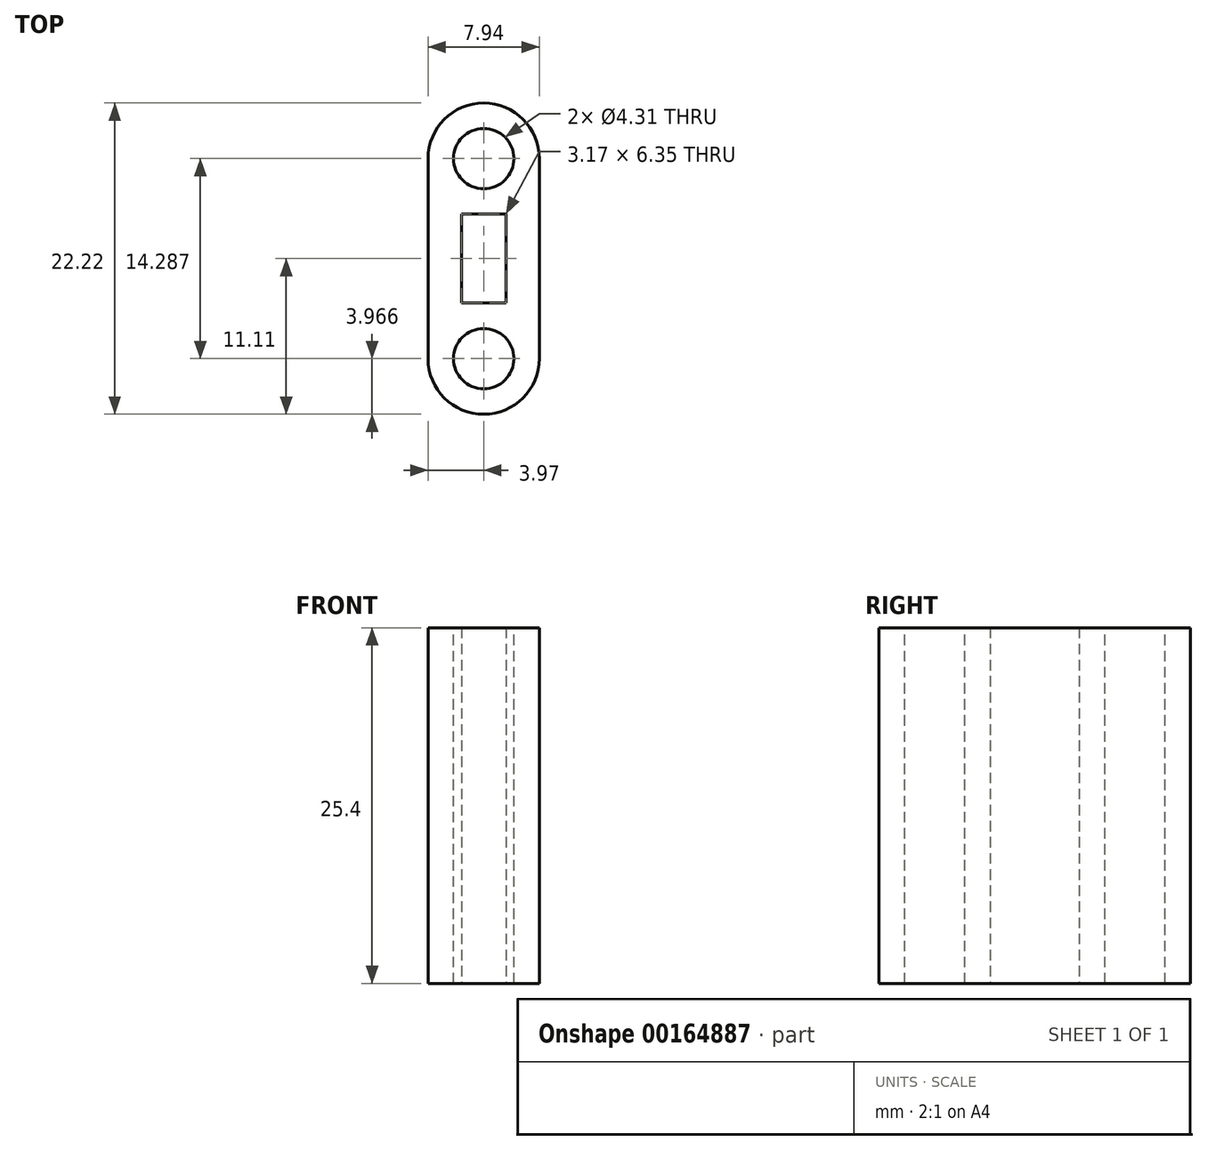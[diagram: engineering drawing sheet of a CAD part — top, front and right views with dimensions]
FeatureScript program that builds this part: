
annotation { "Feature Type Name" : "Feature", "Feature Type Description" : "" }
export const myFeature = defineFeature(function(context is Context, id is Id, definition is map)
    precondition{}
    {
        {
            var Q0;
            Q0=qCreatedBy(makeId("Top.planeOp"),FACE);
            var sketch = newSketch(context, id + "F0", { "sketchPlane" : qUnion([Q0])});
            skLineSegment(sketch, "E0.bottom", {"start": v(3.97, 11.11) * mm, "end": v(-3.97, 11.11) * mm});
            skLineSegment(sketch, "E0.top", {"start": v(3.97, -11.11) * mm, "end": v(-3.97, -11.11) * mm});
            skLineSegment(sketch, "E0.left", {"start": v(3.97, 11.11) * mm, "end": v(3.97, -11.11) * mm});
            skLineSegment(sketch, "E0.right", {"start": v(-3.97, 11.11) * mm, "end": v(-3.97, -11.11) * mm});
            skPoint(sketch, "E0.middle", {"position": v(0, 0) * mm});
            skLineSegment(sketch, "E1.bottom", {"start": v(1.59, 3.18) * mm, "end": v(-1.59, 3.18) * mm});
            skLineSegment(sketch, "E1.top", {"start": v(1.59, -3.18) * mm, "end": v(-1.59, -3.18) * mm});
            skLineSegment(sketch, "E1.left", {"start": v(1.59, 3.18) * mm, "end": v(1.59, -3.18) * mm});
            skLineSegment(sketch, "E1.right", {"start": v(-1.59, 3.18) * mm, "end": v(-1.59, -3.18) * mm});
            skSolve(sketch);
        }
        {
            var Q0;
            Q0 = qSketchRegion(id + "F0", true);
            extrude(context, id + "F1", {"entities" : qUnion([Q0]), "depth" : 25.4 * mm});
        }
        {
            var Q0;
            Q0=makeQuery(id+"F1.opExtrude","CAP_FACE",FACE,{"disambiguationData":[OSD([sQuery(id+"F0.wireOp",EDGE,"E0.bottom"),sQuery(id+"F0.wireOp",EDGE,"E0.top"),sQuery(id+"F0.wireOp",EDGE,"E0.left"),sQuery(id+"F0.wireOp",EDGE,"E0.right"),sQuery(id+"F0.wireOp",EDGE,"E1.bottom"),sQuery(id+"F0.wireOp",EDGE,"E1.top"),sQuery(id+"F0.wireOp",EDGE,"E1.left"),sQuery(id+"F0.wireOp",EDGE,"E1.right")])],"isStart":false});
            var sketch = newSketch(context, id + "F2", { "sketchPlane" : qUnion([Q0])});
            skLineSegment(sketch, "E2.bottom", {"start": v(0, 11.11) * mm, "end": v(3.97, 11.11) * mm, "construction": true});
            skLineSegment(sketch, "E2.top", {"start": v(0, 7.14) * mm, "end": v(3.97, 7.14) * mm, "construction": true});
            skLineSegment(sketch, "E2.left", {"start": v(0, 11.11) * mm, "end": v(0, 7.14) * mm, "construction": true});
            skLineSegment(sketch, "E2.right", {"start": v(3.97, 11.11) * mm, "end": v(3.97, 7.14) * mm, "construction": true});
            skLineSegment(sketch, "E3.bottom", {"start": v(0, -11.11) * mm, "end": v(3.97, -11.11) * mm, "construction": true});
            skLineSegment(sketch, "E3.top", {"start": v(0, -7.14) * mm, "end": v(3.97, -7.14) * mm, "construction": true});
            skLineSegment(sketch, "E3.left", {"start": v(0, -11.11) * mm, "end": v(0, -7.14) * mm, "construction": true});
            skLineSegment(sketch, "E3.right", {"start": v(3.97, -11.11) * mm, "end": v(3.97, -7.14) * mm, "construction": true});
            skCircle(sketch, "E4", {"center": v(0, 7.14) * mm, "radius": 2.15 * mm});
            skCircle(sketch, "E5", {"center": v(0, -7.14) * mm, "radius": 2.15 * mm});
            skSolve(sketch);
        }
        {
            var Q0;
            Q0 = qSketchRegion(id + "F2", true);
            var Q1;
            Q1=makeQuery(id+"F1.opExtrude","CAP_FACE",FACE,{"disambiguationData":[OSD([sQuery(id+"F0.wireOp",EDGE,"E0.bottom"),sQuery(id+"F0.wireOp",EDGE,"E0.top"),sQuery(id+"F0.wireOp",EDGE,"E0.left"),sQuery(id+"F0.wireOp",EDGE,"E0.right"),sQuery(id+"F0.wireOp",EDGE,"E1.bottom"),sQuery(id+"F0.wireOp",EDGE,"E1.top"),sQuery(id+"F0.wireOp",EDGE,"E1.left"),sQuery(id+"F0.wireOp",EDGE,"E1.right")])],"isStart":true});
            extrude(context, id + "F3", {"entities" : qUnion([Q0]), "operationType" : NewBodyOperationType.REMOVE, "endBound" : BoundingType.UP_TO_SURFACE, "oppositeDirection" : true, "endBoundEntityFace" : qUnion([Q1]), "depth" : 25.4 * mm});
        }
        {
            var Q0;
            Q0=makeQuery(id+"F1.opExtrude","SWEPT_EDGE",EDGE,{"disambiguationData":[OSD([sQuery(id+"F0.wireOp",EDGE,"E0.top"),sQuery(id+"F0.wireOp",EDGE,"E0.right")])]});
            var Q1;
            Q1=makeQuery(id+"F1.opExtrude","SWEPT_EDGE",EDGE,{"disambiguationData":[OSD([sQuery(id+"F0.wireOp",EDGE,"E0.top"),sQuery(id+"F0.wireOp",EDGE,"E0.left")])]});
            var Q2;
            Q2=makeQuery(id+"F1.opExtrude","SWEPT_EDGE",EDGE,{"disambiguationData":[OSD([sQuery(id+"F0.wireOp",EDGE,"E0.bottom"),sQuery(id+"F0.wireOp",EDGE,"E0.left")])]});
            var Q3;
            Q3=makeQuery(id+"F1.opExtrude","SWEPT_EDGE",EDGE,{"disambiguationData":[OSD([sQuery(id+"F0.wireOp",EDGE,"E0.bottom"),sQuery(id+"F0.wireOp",EDGE,"E0.right")])]});
            fillet(context, id + "F4", {"entities" : qUnion([Q0, Q1, Q2, Q3]), "radius" : 3.97 * mm, "tangentPropagation" : true, "allowEdgeOverflow" : false});
        }
    });
